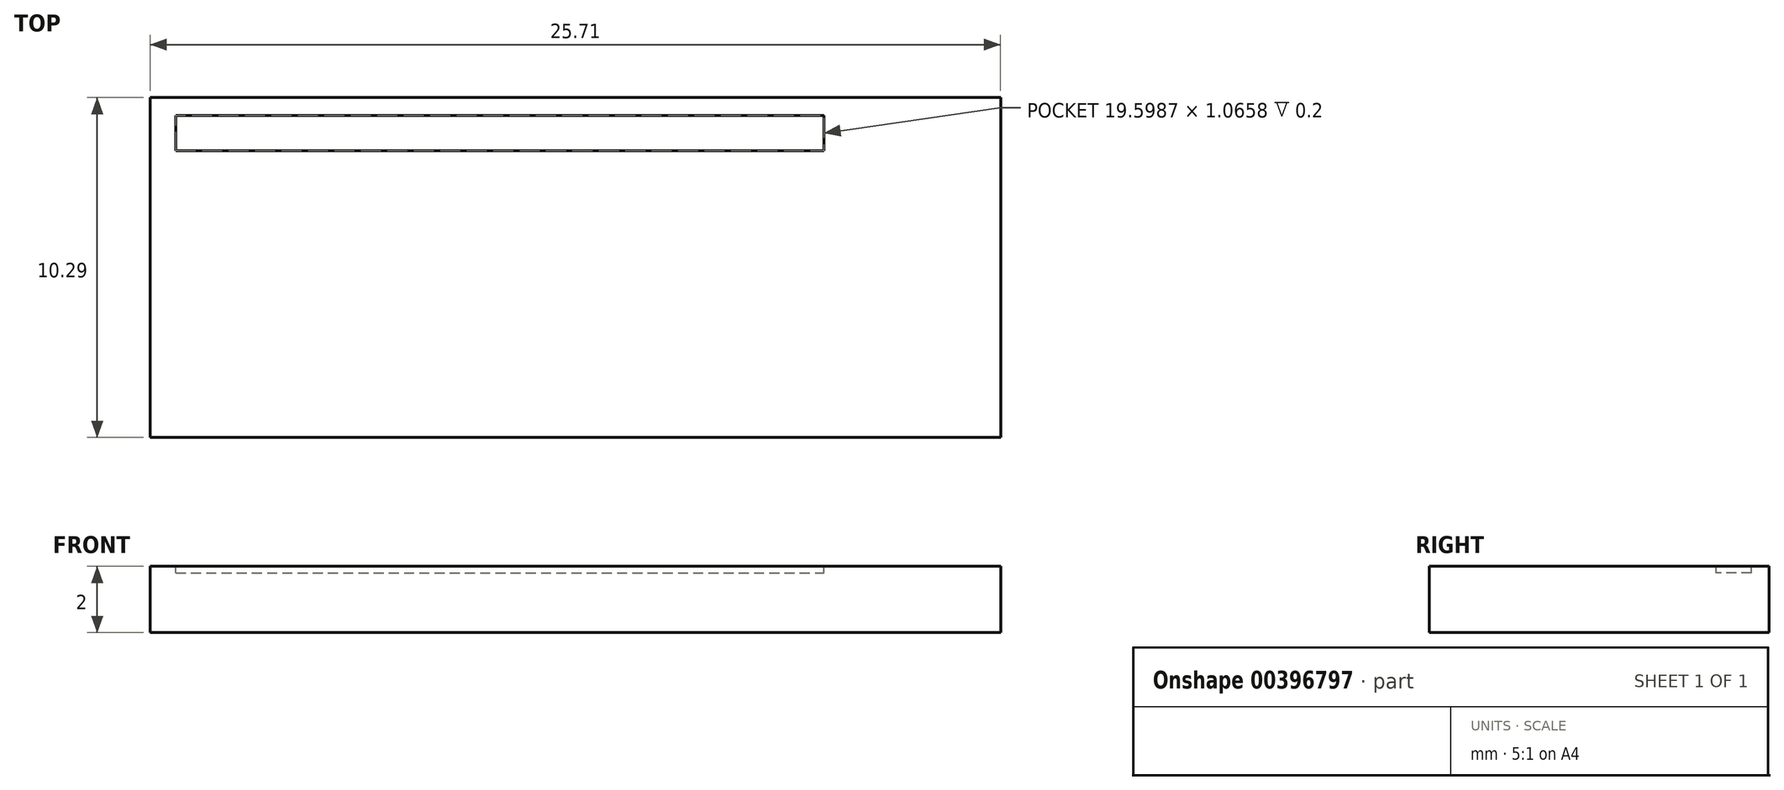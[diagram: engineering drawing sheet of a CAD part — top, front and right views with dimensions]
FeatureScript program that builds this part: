
annotation { "Feature Type Name" : "Feature", "Feature Type Description" : "" }
export const myFeature = defineFeature(function(context is Context, id is Id, definition is map)
    precondition{}
    {
        {
            assignVariable(context, id + "F0", {"name" : "SizeDivision", "anyValue" : 17.5});
        }
        {
            var Q0;
            Q0=qCreatedBy(makeId("Top.planeOp"),FACE);
            var sketch = newSketch(context, id + "F1", { "sketchPlane" : qUnion([Q0])});
            skLineSegment(sketch, "E0.bottom", {"start": v(0, 0) * mm, "end": v(25.71, 0) * mm});
            skLineSegment(sketch, "E0.top", {"start": v(0, -10.29) * mm, "end": v(25.71, -10.29) * mm});
            skLineSegment(sketch, "E0.left", {"start": v(0, 0) * mm, "end": v(0, -10.29) * mm});
            skLineSegment(sketch, "E0.right", {"start": v(25.71, 0) * mm, "end": v(25.71, -10.29) * mm});
            skSolve(sketch);
        }
        {
            var Q0;
            Q0 = qSketchRegion(id + "F1", true);
            extrude(context, id + "F2", {"entities" : qUnion([Q0]), "depth" : (35 / getVariable(context, 'SizeDivision')) * mm});
        }
        {
            var Q0;
            Q0=makeQuery(id+"F2.opExtrude","CAP_FACE",FACE,{"disambiguationData":[OSD([sQuery(id+"F1.wireOp",EDGE,"E0.bottom"),sQuery(id+"F1.wireOp",EDGE,"E0.top"),sQuery(id+"F1.wireOp",EDGE,"E0.left"),sQuery(id+"F1.wireOp",EDGE,"E0.right")])],"isStart":false});
            var sketch = newSketch(context, id + "F3", { "sketchPlane" : qUnion([Q0])});
            skLineSegment(sketch, "E1.bottom", {"start": v(0.78, -0.54) * mm, "end": v(20.38, -0.54) * mm});
            skLineSegment(sketch, "E1.top", {"start": v(0.78, -1.6) * mm, "end": v(20.38, -1.6) * mm});
            skLineSegment(sketch, "E1.left", {"start": v(0.78, -0.54) * mm, "end": v(0.78, -1.6) * mm});
            skLineSegment(sketch, "E1.right", {"start": v(20.38, -0.54) * mm, "end": v(20.38, -1.6) * mm});
            skSolve(sketch);
        }
        {
            var Q0;
            Q0 = qSketchRegion(id + "F3", true);
            extrude(context, id + "F4", {"entities" : qUnion([Q0]), "operationType" : NewBodyOperationType.REMOVE, "oppositeDirection" : true, "depth" : 0.2 * mm});
        }
    });
